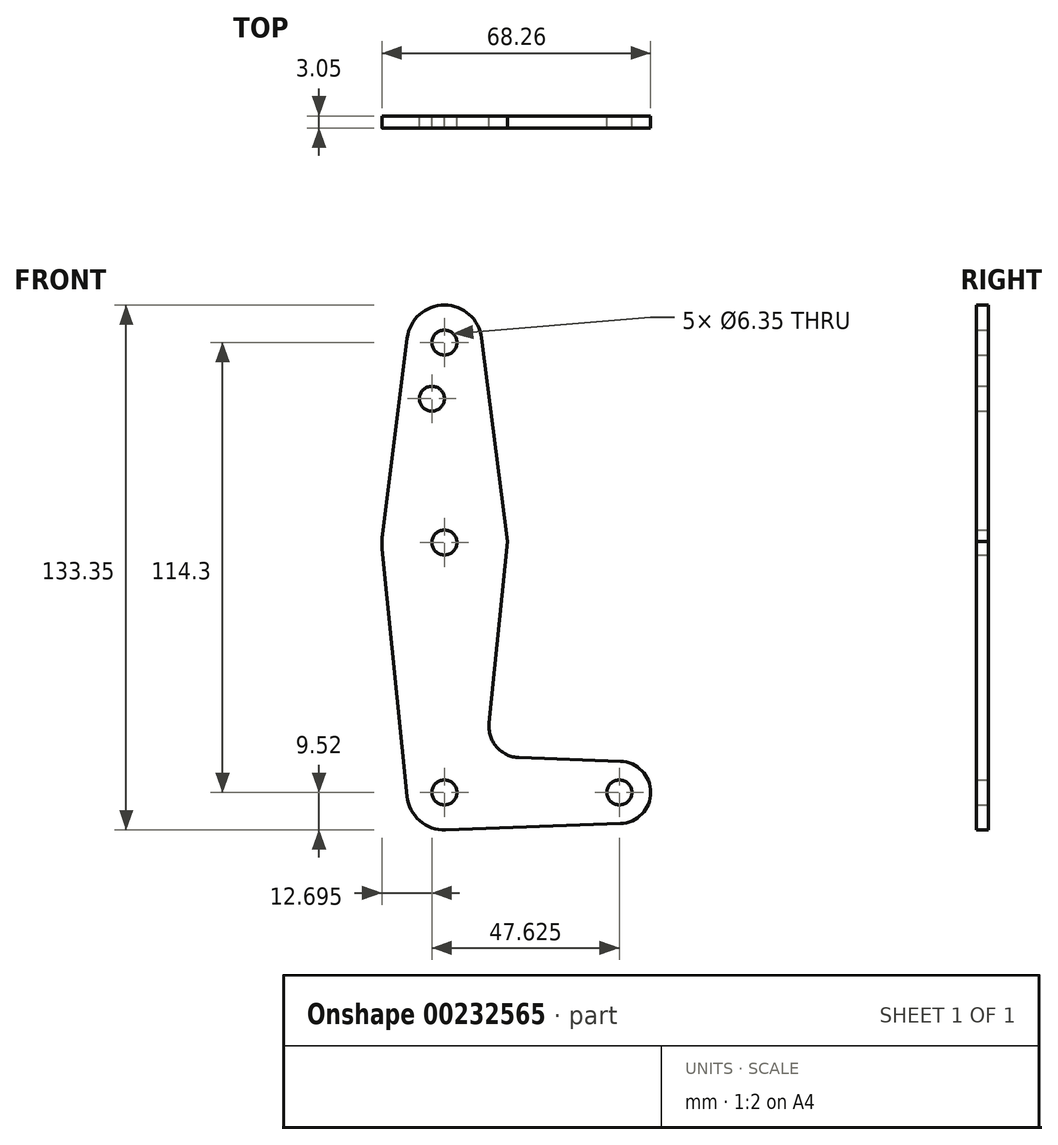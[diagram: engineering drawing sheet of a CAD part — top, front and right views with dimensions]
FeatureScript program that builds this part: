
annotation { "Feature Type Name" : "Feature", "Feature Type Description" : "" }
export const myFeature = defineFeature(function(context is Context, id is Id, definition is map)
    precondition{}
    {
        {
            var Q0;
            Q0=qCreatedBy(makeId("Front.planeOp"),FACE);
            var sketch = newSketch(context, id + "F0", { "sketchPlane" : qUnion([Q0])});
            skLineSegment(sketch, "E0", {"start": v(0, 0) * mm, "end": v(0, 114.3) * mm, "construction": true});
            skLineSegment(sketch, "E1", {"start": v(0, 0) * mm, "end": v(44.45, 0) * mm, "construction": true});
            skCircle(sketch, "E2", {"center": v(0, 114.3) * mm, "radius": 9.53 * mm});
            skCircle(sketch, "E3", {"center": v(0, 0) * mm, "radius": 9.53 * mm});
            skCircle(sketch, "E4", {"center": v(44.45, 0) * mm, "radius": 7.94 * mm});
            skCircle(sketch, "E5", {"center": v(0, 63.5) * mm, "radius": 15.88 * mm});
            skLineSegment(sketch, "E6", {"start": v(-9.45, 115.5) * mm, "end": v(-15.75, 65.48) * mm});
            skLineSegment(sketch, "E7", {"start": v(9.45, 115.5) * mm, "end": v(15.98, 63.7) * mm});
            skLineSegment(sketch, "E8", {"start": v(-15.8, 61.91) * mm, "end": v(-9.48, -0.95) * mm});
            skLineSegment(sketch, "E9", {"start": v(15.98, 63.7) * mm, "end": v(11.34, 17.6) * mm});
            skLineSegment(sketch, "E10", {"start": v(18.97, 8.85) * mm, "end": v(44.73, 7.93) * mm});
            skLineSegment(sketch, "E11", {"start": v(0.34, -9.52) * mm, "end": v(44.73, -7.93) * mm});
            skCircle(sketch, "E12", {"center": v(0, 114.3) * mm, "radius": 3.18 * mm});
            skCircle(sketch, "E13", {"center": v(0, 63.5) * mm, "radius": 3.18 * mm});
            skCircle(sketch, "E14", {"center": v(0, 0) * mm, "radius": 3.18 * mm});
            skCircle(sketch, "E15", {"center": v(44.45, 0) * mm, "radius": 3.18 * mm});
            skCircle(sketch, "E16", {"center": v(-3.18, 100.03) * mm, "radius": 3.18 * mm});
            skArc(sketch, "E17.filletArc", {"start": v(11.34, 17.6) * mm, "mid": v(13.26, 11.57) * mm, "end": v(18.97, 8.85) * mm});
            skSolve(sketch);
        }
        {
            var Q0;
            Q0 = qSketchRegion(id + "F0", true);
            extrude(context, id + "F1", {"entities" : qUnion([Q0]), "depth" : 3.05 * mm});
        }
    });
